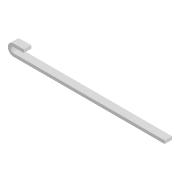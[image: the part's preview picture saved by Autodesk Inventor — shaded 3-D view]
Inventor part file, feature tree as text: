
AUTODESK INVENTOR PART (.ipt)
format: ipt  version: 2020 (Build 240168000, 168)  size: 85,504 bytes
history: native  units: mm
features: extrude x1, sketch x1
ambient origin geometry x8: Origin, YZ Plane, XZ Plane, XY Plane, X Axis, Y Axis, Z Axis, Center Point
bodies: Solid1 (feature_tree)
feature tree (2):
  extrude  "Extrusion1"  Depth=20.0mm
  sketch  "Sketch1"  dims[d0=76.0mm d1=20.0mm d2=20.0mm d4=1000.0mm d5=49.0mm d6=0.0mm d7=68.0mm]
